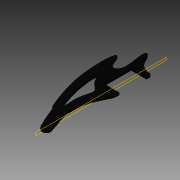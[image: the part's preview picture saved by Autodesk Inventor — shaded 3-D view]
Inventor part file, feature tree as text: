
AUTODESK INVENTOR PART (.ipt)
format: ipt  version: 2015 (Build 190159000, 159)  size: 206,336 bytes
history: native  units: mm
features: extrude x1, sketch x1
ambient origin geometry x8: Origin, YZ Plane, XZ Plane, XY Plane, X Axis, Y Axis, Z Axis, Center Point
bodies: Body1 (feature_tree)
feature tree (2):
  extrude  "Extrusion2"  Depth=9.8044mm
  sketch  "Sketch1"  dims[d0=3.5mm d9=9.8044mm d10=4.4704mm d11=4.4704mm d12=4.4704mm d13=9.8044mm d14=49.1998mm d15=49.11598mm d16=3.5mm d17=0.0mm]
